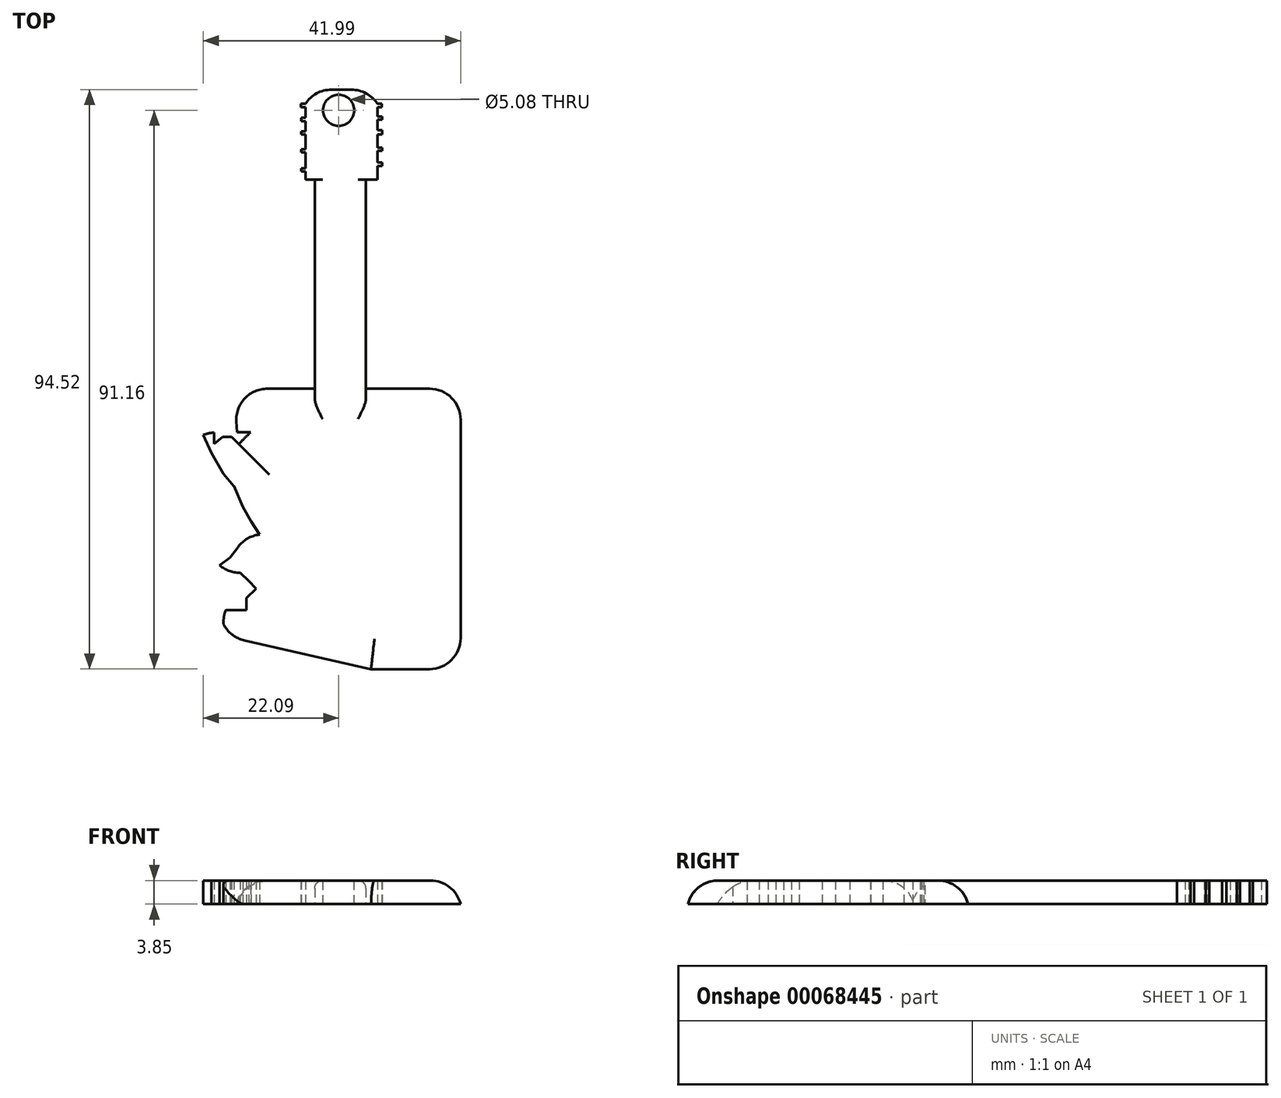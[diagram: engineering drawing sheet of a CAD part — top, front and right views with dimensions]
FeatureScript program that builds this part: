
annotation { "Feature Type Name" : "Feature", "Feature Type Description" : "" }
export const myFeature = defineFeature(function(context is Context, id is Id, definition is map)
    precondition{}
    {
        {
            var Q0;
            Q0=qCreatedBy(makeId("Top.planeOp"),FACE);
            var sketch = newSketch(context, id + "F0", { "sketchPlane" : qUnion([Q0])});
            skLineSegment(sketch, "E0", {"start": v(-16.99, 10.45) * mm, "end": v(19.9, 10.45) * mm});
            skLineSegment(sketch, "E1", {"start": v(19.9, 10.45) * mm, "end": v(19.9, -35.28) * mm});
            skLineSegment(sketch, "E2", {"start": v(19.9, -35.28) * mm, "end": v(5.28, -35.28) * mm});
            skLineSegment(sketch, "E3", {"start": v(5.28, -35.28) * mm, "end": v(-20.63, -29.42) * mm});
            skLineSegment(sketch, "E4", {"start": v(-20.63, -29.42) * mm, "end": v(-18.79, -27.96) * mm});
            skLineSegment(sketch, "E5", {"start": v(-18.79, -27.96) * mm, "end": v(-20.18, -26.2) * mm});
            skLineSegment(sketch, "E6", {"start": v(-20.18, -26.2) * mm, "end": v(-19.48, -25.65) * mm});
            skPoint(sketch, "E6.endSnap0", {"position": v(-19.48, -27.08) * mm});
            skLineSegment(sketch, "E7", {"start": v(-19.48, -25.65) * mm, "end": v(-16.96, -25.65) * mm});
            skLineSegment(sketch, "E8", {"start": v(-16.96, -25.65) * mm, "end": v(-15.05, -25.65) * mm});
            skLineSegment(sketch, "E9", {"start": v(-15.05, -25.65) * mm, "end": v(-15.05, -23.68) * mm});
            skLineSegment(sketch, "E10", {"start": v(-15.05, -23.68) * mm, "end": v(-13.48, -22.2) * mm});
            skLineSegment(sketch, "E11", {"start": v(-13.48, -22.2) * mm, "end": v(-14.71, -20.9) * mm});
            skLineSegment(sketch, "E12", {"start": v(-14.71, -20.9) * mm, "end": v(-16.11, -19.57) * mm});
            skLineSegment(sketch, "E13", {"start": v(-16.11, -19.57) * mm, "end": v(-17.64, -19.57) * mm});
            skLineSegment(sketch, "E14", {"start": v(-17.64, -19.57) * mm, "end": v(-19.42, -19.57) * mm});
            skLineSegment(sketch, "E15", {"start": v(-19.42, -19.57) * mm, "end": v(-19.42, -18.38) * mm});
            skLineSegment(sketch, "E16", {"start": v(-19.42, -18.38) * mm, "end": v(-17.73, -17.1) * mm});
            skLineSegment(sketch, "E17", {"start": v(-17.73, -17.1) * mm, "end": v(-16.37, -15.28) * mm});
            skLineSegment(sketch, "E18", {"start": v(-16.37, -15.28) * mm, "end": v(-14.93, -13.35) * mm});
            skLineSegment(sketch, "E19", {"start": v(-14.93, -13.35) * mm, "end": v(-12.93, -13.35) * mm});
            skLineSegment(sketch, "E20", {"start": v(-12.93, -13.35) * mm, "end": v(-14.29, -11.2) * mm});
            skLineSegment(sketch, "E21", {"start": v(-14.29, -11.2) * mm, "end": v(-15.65, -8.83) * mm});
            skLineSegment(sketch, "E22", {"start": v(-15.65, -8.83) * mm, "end": v(-17.12, -5.41) * mm});
            skLineSegment(sketch, "E23", {"start": v(-17.12, -5.41) * mm, "end": v(-17.12, -5.49) * mm});
            skLineSegment(sketch, "E24", {"start": v(-17.12, -5.49) * mm, "end": v(-18.83, -3.45) * mm});
            skLineSegment(sketch, "E25", {"start": v(-18.83, -3.45) * mm, "end": v(-20.76, 0) * mm});
            skLineSegment(sketch, "E26", {"start": v(-20.76, 0) * mm, "end": v(-20.76, 0) * mm});
            skLineSegment(sketch, "E27", {"start": v(-20.76, 0) * mm, "end": v(-22.09, 2.9) * mm});
            skLineSegment(sketch, "E28", {"start": v(-22.09, 2.9) * mm, "end": v(-22.09, 3.3) * mm});
            skLineSegment(sketch, "E29", {"start": v(-22.09, 3.3) * mm, "end": v(-20.36, 3.3) * mm});
            skLineSegment(sketch, "E30", {"start": v(-20.36, 3.3) * mm, "end": v(-20.36, 1.43) * mm});
            skLineSegment(sketch, "E31", {"start": v(-20.36, 1.43) * mm, "end": v(-20.36, 3.3) * mm});
            skLineSegment(sketch, "E32", {"start": v(-20.36, 1.43) * mm, "end": v(-18.93, 2.61) * mm});
            skLineSegment(sketch, "E33", {"start": v(-18.93, 2.61) * mm, "end": v(-17.5, 2.61) * mm});
            skLineSegment(sketch, "E34", {"start": v(-17.5, 2.61) * mm, "end": v(-16.31, 1.44) * mm});
            skLineSegment(sketch, "E35", {"start": v(-16.31, 1.44) * mm, "end": v(-14.38, 3.37) * mm});
            skLineSegment(sketch, "E36", {"start": v(-14.38, 3.37) * mm, "end": v(-16.62, 3.37) * mm});
            skLineSegment(sketch, "E37", {"start": v(-16.62, 3.37) * mm, "end": v(-16.99, 10.45) * mm});
            skLineSegment(sketch, "E38.bottom", {"start": v(-3.91, 10.45) * mm, "end": v(4.44, 10.45) * mm});
            skLineSegment(sketch, "E38.top", {"start": v(-3.91, 56.05) * mm, "end": v(4.44, 56.05) * mm});
            skLineSegment(sketch, "E38.left", {"start": v(-3.91, 10.45) * mm, "end": v(-3.91, 56.05) * mm});
            skLineSegment(sketch, "E38.right", {"start": v(4.44, 10.45) * mm, "end": v(4.44, 56.05) * mm});
            skLineSegment(sketch, "E39.bottom", {"start": v(-5.43, 44.57) * mm, "end": v(6.31, 44.57) * mm});
            skLineSegment(sketch, "E39.top", {"start": v(-5.43, 59.24) * mm, "end": v(6.31, 59.24) * mm});
            skLineSegment(sketch, "E39.left", {"start": v(-5.43, 44.57) * mm, "end": v(-5.43, 59.24) * mm});
            skLineSegment(sketch, "E39.right", {"start": v(6.31, 44.57) * mm, "end": v(6.31, 59.24) * mm});
            skLineSegment(sketch, "E40.bottom", {"start": v(6.31, 56.4) * mm, "end": v(7.05, 56.4) * mm});
            skLineSegment(sketch, "E40.top", {"start": v(6.31, 56.93) * mm, "end": v(7.05, 56.93) * mm});
            skLineSegment(sketch, "E40.left", {"start": v(6.31, 56.4) * mm, "end": v(6.31, 56.93) * mm});
            skLineSegment(sketch, "E40.right", {"start": v(7.05, 56.4) * mm, "end": v(7.05, 56.93) * mm});
            skLineSegment(sketch, "E41.bottom", {"start": v(6.31, 54.32) * mm, "end": v(7.06, 54.32) * mm});
            skLineSegment(sketch, "E41.top", {"start": v(6.31, 54.86) * mm, "end": v(7.06, 54.86) * mm});
            skLineSegment(sketch, "E41.left", {"start": v(6.31, 54.32) * mm, "end": v(6.31, 54.86) * mm});
            skLineSegment(sketch, "E41.right", {"start": v(7.06, 54.32) * mm, "end": v(7.06, 54.86) * mm});
            skPoint(sketch, "E42.oppositeSnap0", {"position": v(6.31, 51.9) * mm});
            skLineSegment(sketch, "E42.bottom", {"start": v(6.31, 52.63) * mm, "end": v(7.06, 52.63) * mm});
            skLineSegment(sketch, "E42.top", {"start": v(6.31, 51.9) * mm, "end": v(7.06, 51.9) * mm});
            skLineSegment(sketch, "E42.left", {"start": v(6.31, 52.63) * mm, "end": v(6.31, 51.9) * mm});
            skLineSegment(sketch, "E42.right", {"start": v(7.06, 52.63) * mm, "end": v(7.06, 51.9) * mm});
            skLineSegment(sketch, "E43.bottom", {"start": v(6.31, 49.8) * mm, "end": v(7.06, 49.8) * mm});
            skLineSegment(sketch, "E43.top", {"start": v(6.31, 49.27) * mm, "end": v(7.06, 49.27) * mm});
            skLineSegment(sketch, "E43.left", {"start": v(6.31, 49.8) * mm, "end": v(6.31, 49.27) * mm});
            skLineSegment(sketch, "E43.right", {"start": v(7.06, 49.8) * mm, "end": v(7.06, 49.27) * mm});
            skLineSegment(sketch, "E44.bottom", {"start": v(6.31, 47.34) * mm, "end": v(7.06, 47.34) * mm});
            skLineSegment(sketch, "E44.top", {"start": v(6.31, 46.78) * mm, "end": v(7.06, 46.78) * mm});
            skLineSegment(sketch, "E44.left", {"start": v(6.31, 47.34) * mm, "end": v(6.31, 46.78) * mm});
            skLineSegment(sketch, "E44.right", {"start": v(7.06, 47.34) * mm, "end": v(7.06, 46.78) * mm});
            skLineSegment(sketch, "E45.bottom", {"start": v(-5.43, 56.95) * mm, "end": v(-6.17, 56.95) * mm});
            skLineSegment(sketch, "E45.top", {"start": v(-5.43, 56.4) * mm, "end": v(-6.17, 56.4) * mm});
            skLineSegment(sketch, "E45.left", {"start": v(-5.43, 56.95) * mm, "end": v(-5.43, 56.4) * mm});
            skLineSegment(sketch, "E45.right", {"start": v(-6.17, 56.95) * mm, "end": v(-6.17, 56.4) * mm});
            skLineSegment(sketch, "E46.bottom", {"start": v(-5.43, 54.64) * mm, "end": v(-6.12, 54.64) * mm});
            skLineSegment(sketch, "E46.top", {"start": v(-5.43, 54.12) * mm, "end": v(-6.12, 54.12) * mm});
            skLineSegment(sketch, "E46.left", {"start": v(-5.43, 54.64) * mm, "end": v(-5.43, 54.12) * mm});
            skLineSegment(sketch, "E46.right", {"start": v(-6.12, 54.64) * mm, "end": v(-6.12, 54.12) * mm});
            skLineSegment(sketch, "E47.bottom", {"start": v(-5.43, 51.9) * mm, "end": v(-6.1, 51.9) * mm});
            skLineSegment(sketch, "E47.top", {"start": v(-5.43, 52.46) * mm, "end": v(-6.1, 52.46) * mm});
            skLineSegment(sketch, "E47.left", {"start": v(-5.43, 51.9) * mm, "end": v(-5.43, 52.46) * mm});
            skLineSegment(sketch, "E47.right", {"start": v(-6.1, 51.9) * mm, "end": v(-6.1, 52.46) * mm});
            skLineSegment(sketch, "E48.bottom", {"start": v(-5.43, 49.01) * mm, "end": v(-6.09, 49.01) * mm});
            skLineSegment(sketch, "E48.top", {"start": v(-5.43, 49.54) * mm, "end": v(-6.09, 49.54) * mm});
            skLineSegment(sketch, "E48.left", {"start": v(-5.43, 49.01) * mm, "end": v(-5.43, 49.54) * mm});
            skLineSegment(sketch, "E48.right", {"start": v(-6.09, 49.01) * mm, "end": v(-6.09, 49.54) * mm});
            skLineSegment(sketch, "E49.bottom", {"start": v(-5.43, 45.9) * mm, "end": v(-6.12, 45.9) * mm});
            skLineSegment(sketch, "E49.top", {"start": v(-5.43, 46.42) * mm, "end": v(-6.12, 46.42) * mm});
            skLineSegment(sketch, "E49.left", {"start": v(-5.43, 45.9) * mm, "end": v(-5.43, 46.42) * mm});
            skLineSegment(sketch, "E49.right", {"start": v(-6.12, 45.9) * mm, "end": v(-6.12, 46.42) * mm});
            skSolve(sketch);
        }
        {
            var Q0;
            Q0 = qSketchRegion(id + "F0", true);
            extrude(context, id + "F1", {"entities" : qUnion([Q0]), "depth" : 3.85 * mm});
        }
        {
            var Q0;
            Q0=makeQuery(id+"F1.opExtrude","CAP_FACE",FACE,{"disambiguationData":[OSD([sQuery(id+"F0.wireOp",EDGE,"E0"),sQuery(id+"F0.wireOp",EDGE,"E1"),sQuery(id+"F0.wireOp",EDGE,"E2"),sQuery(id+"F0.wireOp",EDGE,"E3"),sQuery(id+"F0.wireOp",EDGE,"E4"),sQuery(id+"F0.wireOp",EDGE,"E5"),sQuery(id+"F0.wireOp",EDGE,"E6"),sQuery(id+"F0.wireOp",EDGE,"E7"),sQuery(id+"F0.wireOp",EDGE,"E8"),sQuery(id+"F0.wireOp",EDGE,"E9"),sQuery(id+"F0.wireOp",EDGE,"E10"),sQuery(id+"F0.wireOp",EDGE,"E11"),sQuery(id+"F0.wireOp",EDGE,"E12"),sQuery(id+"F0.wireOp",EDGE,"E13"),sQuery(id+"F0.wireOp",EDGE,"E14"),sQuery(id+"F0.wireOp",EDGE,"E15"),sQuery(id+"F0.wireOp",EDGE,"E16"),sQuery(id+"F0.wireOp",EDGE,"E17"),sQuery(id+"F0.wireOp",EDGE,"E18"),sQuery(id+"F0.wireOp",EDGE,"E19"),sQuery(id+"F0.wireOp",EDGE,"E20"),sQuery(id+"F0.wireOp",EDGE,"E21"),sQuery(id+"F0.wireOp",EDGE,"E22"),sQuery(id+"F0.wireOp",EDGE,"E23"),sQuery(id+"F0.wireOp",EDGE,"E24"),sQuery(id+"F0.wireOp",EDGE,"E25"),sQuery(id+"F0.wireOp",EDGE,"E26"),sQuery(id+"F0.wireOp",EDGE,"E27"),sQuery(id+"F0.wireOp",EDGE,"E28"),sQuery(id+"F0.wireOp",EDGE,"E29"),sQuery(id+"F0.wireOp",EDGE,"E31"),sQuery(id+"F0.wireOp",EDGE,"E32"),sQuery(id+"F0.wireOp",EDGE,"E33"),sQuery(id+"F0.wireOp",EDGE,"E34"),sQuery(id+"F0.wireOp",EDGE,"E35"),sQuery(id+"F0.wireOp",EDGE,"E36"),sQuery(id+"F0.wireOp",EDGE,"E37"),sQuery(id+"F0.wireOp",EDGE,"E38.left"),sQuery(id+"F0.wireOp",EDGE,"E38.right"),sQuery(id+"F0.wireOp",EDGE,"E39.bottom"),sQuery(id+"F0.wireOp",EDGE,"E39.top"),sQuery(id+"F0.wireOp",EDGE,"E39.left"),sQuery(id+"F0.wireOp",EDGE,"E39.right"),sQuery(id+"F0.wireOp",EDGE,"E40.bottom"),sQuery(id+"F0.wireOp",EDGE,"E40.top"),sQuery(id+"F0.wireOp",EDGE,"E40.right"),sQuery(id+"F0.wireOp",EDGE,"E41.bottom"),sQuery(id+"F0.wireOp",EDGE,"E41.top"),sQuery(id+"F0.wireOp",EDGE,"E41.right"),sQuery(id+"F0.wireOp",EDGE,"E42.bottom"),sQuery(id+"F0.wireOp",EDGE,"E42.top"),sQuery(id+"F0.wireOp",EDGE,"E42.right"),sQuery(id+"F0.wireOp",EDGE,"E43.bottom"),sQuery(id+"F0.wireOp",EDGE,"E43.top"),sQuery(id+"F0.wireOp",EDGE,"E43.right"),sQuery(id+"F0.wireOp",EDGE,"E44.bottom"),sQuery(id+"F0.wireOp",EDGE,"E44.top"),sQuery(id+"F0.wireOp",EDGE,"E44.right"),sQuery(id+"F0.wireOp",EDGE,"E45.bottom"),sQuery(id+"F0.wireOp",EDGE,"E45.top"),sQuery(id+"F0.wireOp",EDGE,"E45.right"),sQuery(id+"F0.wireOp",EDGE,"E46.bottom"),sQuery(id+"F0.wireOp",EDGE,"E46.top"),sQuery(id+"F0.wireOp",EDGE,"E46.right"),sQuery(id+"F0.wireOp",EDGE,"E47.bottom"),sQuery(id+"F0.wireOp",EDGE,"E47.top"),sQuery(id+"F0.wireOp",EDGE,"E47.right"),sQuery(id+"F0.wireOp",EDGE,"E48.bottom"),sQuery(id+"F0.wireOp",EDGE,"E48.top"),sQuery(id+"F0.wireOp",EDGE,"E48.right"),sQuery(id+"F0.wireOp",EDGE,"E49.bottom"),sQuery(id+"F0.wireOp",EDGE,"E49.top"),sQuery(id+"F0.wireOp",EDGE,"E49.right")])],"isStart":false});
            var sketch = newSketch(context, id + "F2", { "sketchPlane" : qUnion([Q0])});
            skCircle(sketch, "E50", {"center": v(0, 55.88) * mm, "radius": 2.54 * mm});
            skSolve(sketch);
        }
        {
            var Q0;
            Q0=makeQuery(id+"F1.opExtrude","SWEPT_EDGE",EDGE,{"disambiguationData":[OSD([sQuery(id+"F0.wireOp",EDGE,"E0"),sQuery(id+"F0.wireOp",EDGE,"E1")])]});
            var Q1;
            Q1=makeQuery(id+"F1.opExtrude","SWEPT_EDGE",EDGE,{"disambiguationData":[OSD([sQuery(id+"F0.wireOp",EDGE,"E1"),sQuery(id+"F0.wireOp",EDGE,"E2")])]});
            var Q2;
            Q2=makeQuery(id+"F1.opExtrude","SWEPT_EDGE",EDGE,{"disambiguationData":[OSD([sQuery(id+"F0.wireOp",EDGE,"E5"),sQuery(id+"F0.wireOp",EDGE,"E6")])]});
            var Q3;
            Q3=makeQuery(id+"F1.opExtrude","SWEPT_EDGE",EDGE,{"disambiguationData":[OSD([sQuery(id+"F0.wireOp",EDGE,"E3"),sQuery(id+"F0.wireOp",EDGE,"E4")])]});
            var Q4;
            Q4=makeQuery(id+"F1.opExtrude","SWEPT_EDGE",EDGE,{"disambiguationData":[OSD([sQuery(id+"F0.wireOp",EDGE,"E14"),sQuery(id+"F0.wireOp",EDGE,"E15")])]});
            var Q5;
            Q5=makeQuery(id+"F1.opExtrude","SWEPT_EDGE",EDGE,{"disambiguationData":[OSD([sQuery(id+"F0.wireOp",EDGE,"E28"),sQuery(id+"F0.wireOp",EDGE,"E29")])]});
            var Q6;
            Q6=makeQuery(id+"F1.opExtrude","SWEPT_EDGE",EDGE,{"disambiguationData":[OSD([sQuery(id+"F0.wireOp",EDGE,"E18"),sQuery(id+"F0.wireOp",EDGE,"E19")])]});
            var Q7;
            Q7=makeQuery(id+"F1.opExtrude","SWEPT_EDGE",EDGE,{"disambiguationData":[OSD([sQuery(id+"F0.wireOp",EDGE,"E0"),sQuery(id+"F0.wireOp",EDGE,"E37")])]});
            var Q8;
            Q8=makeQuery(id+"F1.opExtrude","SWEPT_EDGE",EDGE,{"disambiguationData":[OSD([sQuery(id+"F0.wireOp",EDGE,"E39.top"),sQuery(id+"F0.wireOp",EDGE,"E39.left")])]});
            var Q9;
            Q9=makeQuery(id+"F1.opExtrude","SWEPT_EDGE",EDGE,{"disambiguationData":[OSD([sQuery(id+"F0.wireOp",EDGE,"E39.top"),sQuery(id+"F0.wireOp",EDGE,"E39.right")])]});
            fillet(context, id + "F3", {"entities" : qUnion([Q0, Q1, Q2, Q3, Q4, Q5, Q6, Q7, Q8, Q9]), "radius" : 5.08 * mm, "tangentPropagation" : true, "allowEdgeOverflow" : false});
        }
        {
            var Q0;
            Q0=makeQuery(id+"F1.opExtrude","CAP_EDGE",EDGE,{"disambiguationData":[OSD([sQuery(id+"F0.wireOp",EDGE,"E1")])],"isStart":false});
            var Q1;
            {var subQ0=sQuery(id+"F0.wireOp",EDGE,"E0");Q1=makeQuery(id+"F1.opExtrude","CAP_EDGE",EDGE,{"disambiguationData":[OSD([subQ0]),TDD([makeQuery(id+"F0.imprint","IMPRINT",EDGE,{"disambiguationData":[TD([[makeQuery(id+"F0.imprint","INTERSECT",VERTEX,{"derivedFrom":[subQ0,sQuery(id+"F0.wireOp",EDGE,"E37")]}),-1.0]])],"derivedFrom":subQ0})])],"isStart":false});}
            var Q2;
            {var subQ0=sQuery(id+"F0.wireOp",EDGE,"E4");var subQ1=sQuery(id+"F0.wireOp",EDGE,"E3");Q2=makeQuery(id+"F3.opFillet","BLEND_EDGE",EDGE,{"blendedFrom":[makeQuery(id+"F1.opExtrude","SWEPT_EDGE",EDGE,{"disambiguationData":[OSD([subQ1,subQ0])]}),makeQuery(id+"F1.opExtrude","CAP_FACE",FACE,{"disambiguationData":[OSD([sQuery(id+"F0.wireOp",EDGE,"E0"),sQuery(id+"F0.wireOp",EDGE,"E1"),sQuery(id+"F0.wireOp",EDGE,"E2"),subQ1,subQ0,sQuery(id+"F0.wireOp",EDGE,"E5"),sQuery(id+"F0.wireOp",EDGE,"E6"),sQuery(id+"F0.wireOp",EDGE,"E7"),sQuery(id+"F0.wireOp",EDGE,"E8"),sQuery(id+"F0.wireOp",EDGE,"E9"),sQuery(id+"F0.wireOp",EDGE,"E10"),sQuery(id+"F0.wireOp",EDGE,"E11"),sQuery(id+"F0.wireOp",EDGE,"E12"),sQuery(id+"F0.wireOp",EDGE,"E13"),sQuery(id+"F0.wireOp",EDGE,"E14"),sQuery(id+"F0.wireOp",EDGE,"E15"),sQuery(id+"F0.wireOp",EDGE,"E16"),sQuery(id+"F0.wireOp",EDGE,"E17"),sQuery(id+"F0.wireOp",EDGE,"E18"),sQuery(id+"F0.wireOp",EDGE,"E19"),sQuery(id+"F0.wireOp",EDGE,"E20"),sQuery(id+"F0.wireOp",EDGE,"E21"),sQuery(id+"F0.wireOp",EDGE,"E22"),sQuery(id+"F0.wireOp",EDGE,"E23"),sQuery(id+"F0.wireOp",EDGE,"E24"),sQuery(id+"F0.wireOp",EDGE,"E25"),sQuery(id+"F0.wireOp",EDGE,"E27"),sQuery(id+"F0.wireOp",EDGE,"E28"),sQuery(id+"F0.wireOp",EDGE,"E29"),sQuery(id+"F0.wireOp",EDGE,"E31"),sQuery(id+"F0.wireOp",EDGE,"E32"),sQuery(id+"F0.wireOp",EDGE,"E33"),sQuery(id+"F0.wireOp",EDGE,"E34"),sQuery(id+"F0.wireOp",EDGE,"E35"),sQuery(id+"F0.wireOp",EDGE,"E36"),sQuery(id+"F0.wireOp",EDGE,"E37"),sQuery(id+"F0.wireOp",EDGE,"E38.left"),sQuery(id+"F0.wireOp",EDGE,"E38.right"),sQuery(id+"F0.wireOp",EDGE,"E39.bottom"),sQuery(id+"F0.wireOp",EDGE,"E39.top"),sQuery(id+"F0.wireOp",EDGE,"E39.left"),sQuery(id+"F0.wireOp",EDGE,"E39.right"),sQuery(id+"F0.wireOp",EDGE,"E40.bottom"),sQuery(id+"F0.wireOp",EDGE,"E40.top"),sQuery(id+"F0.wireOp",EDGE,"E40.right"),sQuery(id+"F0.wireOp",EDGE,"E41.bottom"),sQuery(id+"F0.wireOp",EDGE,"E41.top"),sQuery(id+"F0.wireOp",EDGE,"E41.right"),sQuery(id+"F0.wireOp",EDGE,"E42.bottom"),sQuery(id+"F0.wireOp",EDGE,"E42.top"),sQuery(id+"F0.wireOp",EDGE,"E42.right"),sQuery(id+"F0.wireOp",EDGE,"E43.bottom"),sQuery(id+"F0.wireOp",EDGE,"E43.top"),sQuery(id+"F0.wireOp",EDGE,"E43.right"),sQuery(id+"F0.wireOp",EDGE,"E44.bottom"),sQuery(id+"F0.wireOp",EDGE,"E44.top"),sQuery(id+"F0.wireOp",EDGE,"E44.right"),sQuery(id+"F0.wireOp",EDGE,"E45.bottom"),sQuery(id+"F0.wireOp",EDGE,"E45.top"),sQuery(id+"F0.wireOp",EDGE,"E45.right"),sQuery(id+"F0.wireOp",EDGE,"E46.bottom"),sQuery(id+"F0.wireOp",EDGE,"E46.top"),sQuery(id+"F0.wireOp",EDGE,"E46.right"),sQuery(id+"F0.wireOp",EDGE,"E47.bottom"),sQuery(id+"F0.wireOp",EDGE,"E47.top"),sQuery(id+"F0.wireOp",EDGE,"E47.right"),sQuery(id+"F0.wireOp",EDGE,"E48.bottom"),sQuery(id+"F0.wireOp",EDGE,"E48.top"),sQuery(id+"F0.wireOp",EDGE,"E48.right"),sQuery(id+"F0.wireOp",EDGE,"E49.bottom"),sQuery(id+"F0.wireOp",EDGE,"E49.top"),sQuery(id+"F0.wireOp",EDGE,"E49.right")])],"isStart":false})],"blendedInto":[makeQuery(id+"F1.opExtrude","CAP_FACE",FACE,{"disambiguationData":[OSD([sQuery(id+"F0.wireOp",EDGE,"E0"),sQuery(id+"F0.wireOp",EDGE,"E1"),sQuery(id+"F0.wireOp",EDGE,"E2"),subQ1,subQ0,sQuery(id+"F0.wireOp",EDGE,"E5"),sQuery(id+"F0.wireOp",EDGE,"E6"),sQuery(id+"F0.wireOp",EDGE,"E7"),sQuery(id+"F0.wireOp",EDGE,"E8"),sQuery(id+"F0.wireOp",EDGE,"E9"),sQuery(id+"F0.wireOp",EDGE,"E10"),sQuery(id+"F0.wireOp",EDGE,"E11"),sQuery(id+"F0.wireOp",EDGE,"E12"),sQuery(id+"F0.wireOp",EDGE,"E13"),sQuery(id+"F0.wireOp",EDGE,"E14"),sQuery(id+"F0.wireOp",EDGE,"E15"),sQuery(id+"F0.wireOp",EDGE,"E16"),sQuery(id+"F0.wireOp",EDGE,"E17"),sQuery(id+"F0.wireOp",EDGE,"E18"),sQuery(id+"F0.wireOp",EDGE,"E19"),sQuery(id+"F0.wireOp",EDGE,"E20"),sQuery(id+"F0.wireOp",EDGE,"E21"),sQuery(id+"F0.wireOp",EDGE,"E22"),sQuery(id+"F0.wireOp",EDGE,"E23"),sQuery(id+"F0.wireOp",EDGE,"E24"),sQuery(id+"F0.wireOp",EDGE,"E25"),sQuery(id+"F0.wireOp",EDGE,"E27"),sQuery(id+"F0.wireOp",EDGE,"E28"),sQuery(id+"F0.wireOp",EDGE,"E29"),sQuery(id+"F0.wireOp",EDGE,"E31"),sQuery(id+"F0.wireOp",EDGE,"E32"),sQuery(id+"F0.wireOp",EDGE,"E33"),sQuery(id+"F0.wireOp",EDGE,"E34"),sQuery(id+"F0.wireOp",EDGE,"E35"),sQuery(id+"F0.wireOp",EDGE,"E36"),sQuery(id+"F0.wireOp",EDGE,"E37"),sQuery(id+"F0.wireOp",EDGE,"E38.left"),sQuery(id+"F0.wireOp",EDGE,"E38.right"),sQuery(id+"F0.wireOp",EDGE,"E39.bottom"),sQuery(id+"F0.wireOp",EDGE,"E39.top"),sQuery(id+"F0.wireOp",EDGE,"E39.left"),sQuery(id+"F0.wireOp",EDGE,"E39.right"),sQuery(id+"F0.wireOp",EDGE,"E40.bottom"),sQuery(id+"F0.wireOp",EDGE,"E40.top"),sQuery(id+"F0.wireOp",EDGE,"E40.right"),sQuery(id+"F0.wireOp",EDGE,"E41.bottom"),sQuery(id+"F0.wireOp",EDGE,"E41.top"),sQuery(id+"F0.wireOp",EDGE,"E41.right"),sQuery(id+"F0.wireOp",EDGE,"E42.bottom"),sQuery(id+"F0.wireOp",EDGE,"E42.top"),sQuery(id+"F0.wireOp",EDGE,"E42.right"),sQuery(id+"F0.wireOp",EDGE,"E43.bottom"),sQuery(id+"F0.wireOp",EDGE,"E43.top"),sQuery(id+"F0.wireOp",EDGE,"E43.right"),sQuery(id+"F0.wireOp",EDGE,"E44.bottom"),sQuery(id+"F0.wireOp",EDGE,"E44.top"),sQuery(id+"F0.wireOp",EDGE,"E44.right"),sQuery(id+"F0.wireOp",EDGE,"E45.bottom"),sQuery(id+"F0.wireOp",EDGE,"E45.top"),sQuery(id+"F0.wireOp",EDGE,"E45.right"),sQuery(id+"F0.wireOp",EDGE,"E46.bottom"),sQuery(id+"F0.wireOp",EDGE,"E46.top"),sQuery(id+"F0.wireOp",EDGE,"E46.right"),sQuery(id+"F0.wireOp",EDGE,"E47.bottom"),sQuery(id+"F0.wireOp",EDGE,"E47.top"),sQuery(id+"F0.wireOp",EDGE,"E47.right"),sQuery(id+"F0.wireOp",EDGE,"E48.bottom"),sQuery(id+"F0.wireOp",EDGE,"E48.top"),sQuery(id+"F0.wireOp",EDGE,"E48.right"),sQuery(id+"F0.wireOp",EDGE,"E49.bottom"),sQuery(id+"F0.wireOp",EDGE,"E49.top"),sQuery(id+"F0.wireOp",EDGE,"E49.right")])],"isStart":false})]});}
            fillet(context, id + "F4", {"entities" : qUnion([Q0, Q1, Q2]), "radius" : 5.08 * mm, "tangentPropagation" : true, "allowEdgeOverflow" : false});
        }
        {
            var Q0;
            Q0=makeQuery(id+"F1.opExtrude","CAP_EDGE",EDGE,{"disambiguationData":[OSD([sQuery(id+"F0.wireOp",EDGE,"E38.right")])],"isStart":false});
            var Q1;
            Q1=makeQuery(id+"F1.opExtrude","CAP_EDGE",EDGE,{"disambiguationData":[OSD([sQuery(id+"F0.wireOp",EDGE,"E38.left")])],"isStart":false});
            fillet(context, id + "F5", {"entities" : qUnion([Q0, Q1]), "radius" : 1.27 * mm, "tangentPropagation" : true, "allowEdgeOverflow" : false});
        }
        {
            var Q0;
            Q0=makeQuery(id+"F2.imprint","IMPRINT",FACE,{"disambiguationData":[TD([[makeQuery(id+"F2.imprint","IMPRINT",EDGE,{"derivedFrom":sQuery(id+"F2.wireOp",EDGE,"E50")}),1.0]])]});
            extrude(context, id + "F6", {"entities" : qUnion([Q0]), "operationType" : NewBodyOperationType.REMOVE, "oppositeDirection" : true, "depth" : 25.4 * mm});
        }
    });
